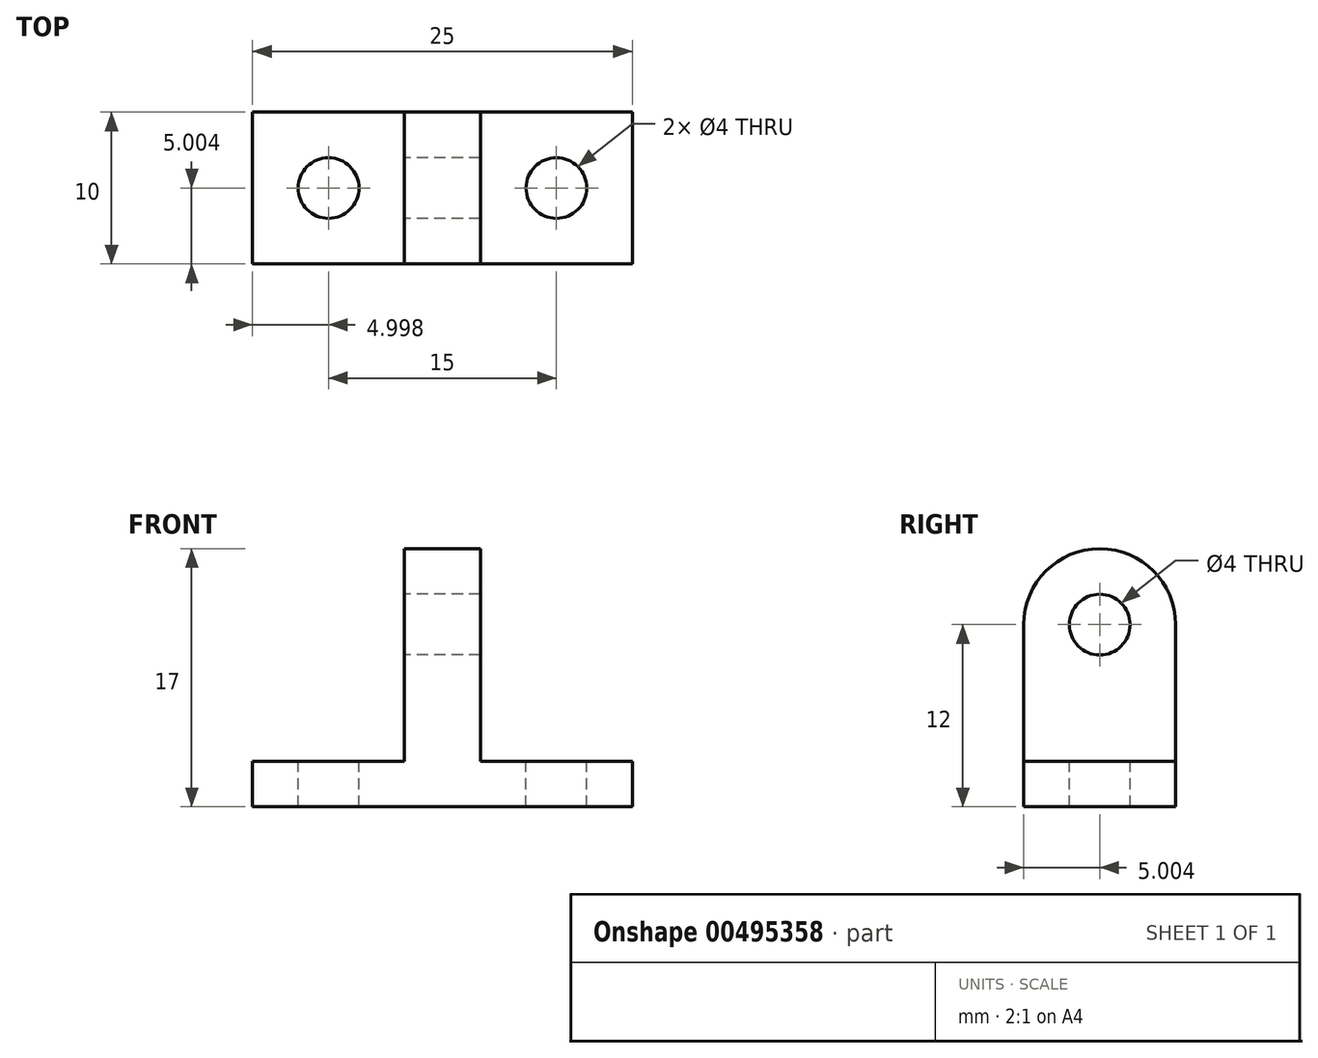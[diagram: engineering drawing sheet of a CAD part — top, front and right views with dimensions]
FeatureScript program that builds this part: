
annotation { "Feature Type Name" : "Feature", "Feature Type Description" : "" }
export const myFeature = defineFeature(function(context is Context, id is Id, definition is map)
    precondition{}
    {
        {
            var Q0;
            Q0=qCreatedBy(makeId("Top.planeOp"),FACE);
            var sketch = newSketch(context, id + "F0", { "sketchPlane" : qUnion([Q0])});
            skLineSegment(sketch, "E0.bottom", {"start": v(-54.6, -2.19) * mm, "end": v(-29.6, -2.19) * mm});
            skLineSegment(sketch, "E0.top", {"start": v(-54.6, -12.19) * mm, "end": v(-29.6, -12.19) * mm});
            skLineSegment(sketch, "E0.left", {"start": v(-54.6, -2.19) * mm, "end": v(-54.6, -12.19) * mm});
            skLineSegment(sketch, "E0.right", {"start": v(-29.6, -2.19) * mm, "end": v(-29.6, -12.19) * mm});
            skSolve(sketch);
        }
        {
            var Q0;
            Q0=makeQuery(id+"F0.imprint","IMPRINT",FACE,{"disambiguationData":[TD([[makeQuery(id+"F0.imprint","IMPRINT",EDGE,{"derivedFrom":sQuery(id+"F0.wireOp",EDGE,"E0.bottom")}),-1.0]])]});
            extrude(context, id + "F1", {"entities" : qUnion([Q0]), "flatOperationType" : FlatOperationType.REMOVE, "offsetDistance" : 25 * mm, "depth" : 3 * mm, "domain" : OperationDomain.MODEL});
        }
        {
            var Q0;
            Q0=makeQuery(id+"F1.opExtrude","CAP_FACE",FACE,{"disambiguationData":[OSD([sQuery(id+"F0.wireOp",EDGE,"E0.bottom"),sQuery(id+"F0.wireOp",EDGE,"E0.top"),sQuery(id+"F0.wireOp",EDGE,"E0.left"),sQuery(id+"F0.wireOp",EDGE,"E0.right")])],"isStart":false});
            var sketch = newSketch(context, id + "F2", { "sketchPlane" : qUnion([Q0])});
            skLineSegment(sketch, "E1.bottom", {"start": v(-44.6, -2.19) * mm, "end": v(-39.6, -2.19) * mm});
            skLineSegment(sketch, "E1.top", {"start": v(-44.6, -12.19) * mm, "end": v(-39.6, -12.19) * mm});
            skLineSegment(sketch, "E1.left", {"start": v(-44.6, -2.19) * mm, "end": v(-44.6, -12.19) * mm});
            skLineSegment(sketch, "E1.right", {"start": v(-39.6, -2.19) * mm, "end": v(-39.6, -12.19) * mm});
            skSolve(sketch);
        }
        {
            var Q0;
            Q0=makeQuery(id+"F2.imprint","IMPRINT",FACE,{"disambiguationData":[TD([[makeQuery(id+"F2.imprint","IMPRINT",EDGE,{"derivedFrom":sQuery(id+"F2.wireOp",EDGE,"E1.bottom")}),-1.0]])]});
            extrude(context, id + "F3", {"entities" : qUnion([Q0]), "operationType" : NewBodyOperationType.ADD, "depth" : 14 * mm});
        }
        {
            var Q0;
            {var subQ0=sQuery(id+"F0.wireOp",EDGE,"E0.left");var subQ1=sQuery(id+"F0.wireOp",EDGE,"E0.top");var subQ2=sQuery(id+"F0.wireOp",EDGE,"E0.bottom");Q0=makeQuery(id+"F3.boolean.opBoolean","SPLIT",FACE,{"disambiguationData":[TD([makeQuery(id+"F1.opExtrude","SWEPT_FACE",FACE,{"disambiguationData":[OSD([subQ0])]})])],"derivedFrom":makeQuery(id+"F1.opExtrude","CAP_FACE",FACE,{"disambiguationData":[OSD([subQ2,subQ1,subQ0,sQuery(id+"F0.wireOp",EDGE,"E0.right")])],"isStart":false})});}
            var sketch = newSketch(context, id + "F4", { "sketchPlane" : qUnion([Q0])});
            skCircle(sketch, "E2", {"center": v(-49.6, -7.19) * mm, "radius": 2 * mm});
            skCircle(sketch, "E3", {"center": v(-34.6, -7.19) * mm, "radius": 2 * mm});
            skSolve(sketch);
        }
        {
            var Q0;
            Q0=makeQuery(id+"F3.opExtrude","CAP_EDGE",EDGE,{"disambiguationData":[OSD([sQuery(id+"F2.wireOp",EDGE,"E1.top")])],"isStart":false});
            var Q1;
            Q1=makeQuery(id+"F3.opExtrude","CAP_EDGE",EDGE,{"disambiguationData":[OSD([sQuery(id+"F2.wireOp",EDGE,"E1.bottom")])],"isStart":false});
            fillet(context, id + "F5", {"entities" : qUnion([Q0, Q1]), "radius" : 5 * mm, "tangentPropagation" : true, "allowEdgeOverflow" : false});
        }
        {
            var Q0;
            Q0=makeQuery(id+"F3.opExtrude","SWEPT_FACE",FACE,{"disambiguationData":[OSD([sQuery(id+"F2.wireOp",EDGE,"E1.left")])]});
            var sketch = newSketch(context, id + "F6", { "sketchPlane" : qUnion([Q0])});
            skCircle(sketch, "E4", {"center": v(7.19, 12) * mm, "radius": 2 * mm});
            skSolve(sketch);
        }
        {
            var Q0;
            Q0=makeQuery(id+"F4.imprint","IMPRINT",FACE,{"disambiguationData":[TD([[makeQuery(id+"F4.imprint","IMPRINT",EDGE,{"derivedFrom":sQuery(id+"F4.wireOp",EDGE,"E2")}),1.0]])]});
            var Q1;
            Q1=makeQuery(id+"F4.imprint","IMPRINT",FACE,{"disambiguationData":[TD([[makeQuery(id+"F4.imprint","IMPRINT",EDGE,{"derivedFrom":sQuery(id+"F4.wireOp",EDGE,"E3")}),1.0]])]});
            extrude(context, id + "F7", {"entities" : qUnion([Q0, Q1]), "operationType" : NewBodyOperationType.REMOVE, "oppositeDirection" : true, "depth" : 3 * mm});
        }
        {
            var Q0;
            Q0=makeQuery(id+"F6.imprint","IMPRINT",FACE,{"disambiguationData":[TD([[makeQuery(id+"F6.imprint","IMPRINT",EDGE,{"derivedFrom":sQuery(id+"F6.wireOp",EDGE,"E4")}),1.0]])]});
            extrude(context, id + "F8", {"entities" : qUnion([Q0]), "operationType" : NewBodyOperationType.REMOVE, "oppositeDirection" : true, "depth" : 5 * mm});
        }
    });
